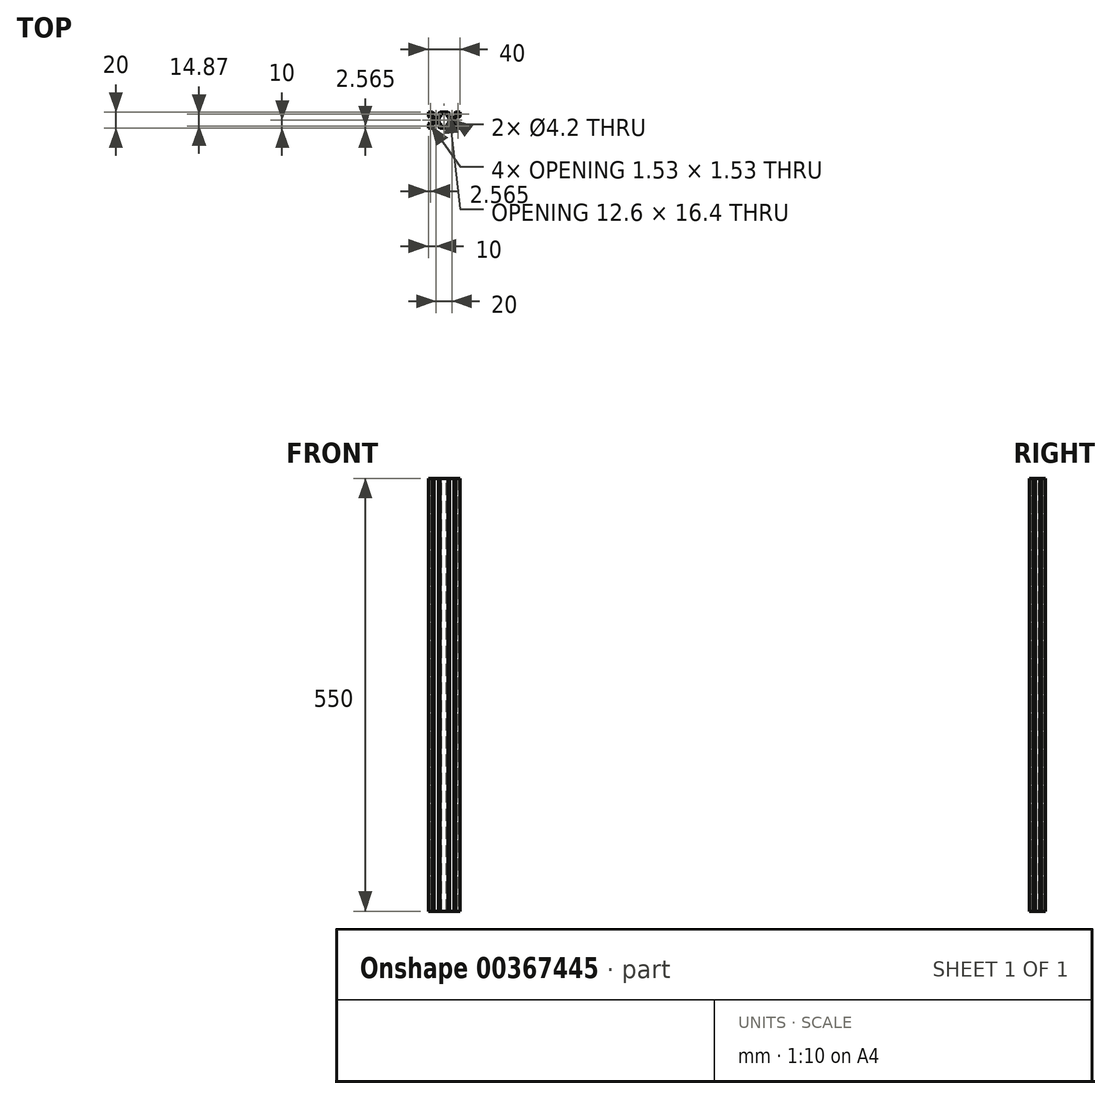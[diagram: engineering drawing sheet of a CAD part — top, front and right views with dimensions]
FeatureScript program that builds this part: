
annotation { "Feature Type Name" : "Feature", "Feature Type Description" : "" }
export const myFeature = defineFeature(function(context is Context, id is Id, definition is map)
    precondition{}
    {
        {
            var Q0;
            Q0=qCreatedBy(makeId("Top.planeOp"),FACE);
            var sketch = newSketch(context, id + "F0", { "sketchPlane" : qUnion([Q0])});
            skLineSegment(sketch, "E0.bottom", {"start": v(0, 0) * mm, "end": v(5.2, 0) * mm});
            skLineSegment(sketch, "E0.top", {"start": v(0, 20) * mm, "end": v(5.2, 20) * mm});
            skLineSegment(sketch, "E0.left", {"start": v(0, 0) * mm, "end": v(0, 5.2) * mm});
            skLineSegment(sketch, "E0.right", {"start": v(40, 0) * mm, "end": v(40, 5.2) * mm});
            skLineSegment(sketch, "E1", {"start": v(33.8, 12.84) * mm, "end": v(33.8, 7.16) * mm});
            skLineSegment(sketch, "E2", {"start": v(33.8, 12.84) * mm, "end": v(36.56, 15.6) * mm});
            skLineSegment(sketch, "E3", {"start": v(33.8, 7.16) * mm, "end": v(36.56, 4.4) * mm});
            skLineSegment(sketch, "E4", {"start": v(36.56, 15.6) * mm, "end": v(38.2, 15.6) * mm});
            skLineSegment(sketch, "E5", {"start": v(36.56, 4.4) * mm, "end": v(38.2, 4.4) * mm});
            skLineSegment(sketch, "E6", {"start": v(38.2, 13) * mm, "end": v(38.2, 15.6) * mm});
            skLineSegment(sketch, "E7", {"start": v(38.2, 7) * mm, "end": v(38.2, 4.4) * mm});
            skLineSegment(sketch, "E8.trimOffspring", {"start": v(40, 14.8) * mm, "end": v(40, 20) * mm});
            skLineSegment(sketch, "E9", {"start": v(33, 18.2) * mm, "end": v(35.6, 18.2) * mm});
            skLineSegment(sketch, "E10", {"start": v(35.6, 18.2) * mm, "end": v(35.6, 16.56) * mm});
            skLineSegment(sketch, "E11", {"start": v(35.6, 16.56) * mm, "end": v(32.84, 13.8) * mm});
            skLineSegment(sketch, "E12", {"start": v(32.84, 13.8) * mm, "end": v(27.16, 13.8) * mm});
            skLineSegment(sketch, "E13", {"start": v(27, 18.2) * mm, "end": v(24.4, 18.2) * mm});
            skLineSegment(sketch, "E14", {"start": v(24.4, 18.2) * mm, "end": v(24.4, 16.56) * mm});
            skLineSegment(sketch, "E15", {"start": v(24.4, 16.56) * mm, "end": v(27.16, 13.8) * mm});
            skLineSegment(sketch, "E16", {"start": v(33, 1.8) * mm, "end": v(35.6, 1.8) * mm});
            skLineSegment(sketch, "E17", {"start": v(35.6, 1.8) * mm, "end": v(35.6, 3.44) * mm});
            skLineSegment(sketch, "E18", {"start": v(35.6, 3.44) * mm, "end": v(32.84, 6.2) * mm});
            skLineSegment(sketch, "E19", {"start": v(32.84, 6.2) * mm, "end": v(27.16, 6.2) * mm});
            skLineSegment(sketch, "E20", {"start": v(27.16, 6.2) * mm, "end": v(24.4, 3.44) * mm});
            skLineSegment(sketch, "E21", {"start": v(24.4, 3.44) * mm, "end": v(24.4, 1.8) * mm});
            skLineSegment(sketch, "E22", {"start": v(24.4, 1.8) * mm, "end": v(27, 1.8) * mm});
            skLineSegment(sketch, "E23.trimOffspring", {"start": v(34.8, 20) * mm, "end": v(40, 20) * mm});
            skLineSegment(sketch, "E24.trimOffspring", {"start": v(34.8, 0) * mm, "end": v(40, 0) * mm});
            skLineSegment(sketch, "E25", {"start": v(7, 18.2) * mm, "end": v(4.4, 18.2) * mm});
            skLineSegment(sketch, "E26", {"start": v(4.4, 18.2) * mm, "end": v(4.4, 16.56) * mm});
            skLineSegment(sketch, "E27", {"start": v(4.4, 16.56) * mm, "end": v(7.16, 13.8) * mm});
            skLineSegment(sketch, "E28", {"start": v(7.16, 13.8) * mm, "end": v(12.84, 13.8) * mm});
            skLineSegment(sketch, "E29", {"start": v(12.84, 13.8) * mm, "end": v(15.6, 16.56) * mm});
            skLineSegment(sketch, "E30", {"start": v(15.6, 16.56) * mm, "end": v(15.6, 18.2) * mm});
            skLineSegment(sketch, "E31", {"start": v(15.6, 18.2) * mm, "end": v(13, 18.2) * mm});
            skLineSegment(sketch, "E32", {"start": v(1.8, 13) * mm, "end": v(1.8, 15.6) * mm});
            skLineSegment(sketch, "E33", {"start": v(1.8, 15.6) * mm, "end": v(3.44, 15.6) * mm});
            skLineSegment(sketch, "E34", {"start": v(3.44, 15.6) * mm, "end": v(6.2, 12.84) * mm});
            skLineSegment(sketch, "E35", {"start": v(6.2, 12.84) * mm, "end": v(6.2, 7.16) * mm});
            skLineSegment(sketch, "E36", {"start": v(6.2, 7.16) * mm, "end": v(3.44, 4.4) * mm});
            skLineSegment(sketch, "E37", {"start": v(3.44, 4.4) * mm, "end": v(1.8, 4.4) * mm});
            skLineSegment(sketch, "E38", {"start": v(1.8, 7) * mm, "end": v(1.8, 4.4) * mm});
            skLineSegment(sketch, "E39", {"start": v(7, 1.8) * mm, "end": v(4.4, 1.8) * mm});
            skLineSegment(sketch, "E40", {"start": v(4.4, 1.8) * mm, "end": v(4.4, 3.44) * mm});
            skLineSegment(sketch, "E41", {"start": v(4.4, 3.44) * mm, "end": v(7.16, 6.2) * mm});
            skLineSegment(sketch, "E42", {"start": v(7.16, 6.2) * mm, "end": v(12.84, 6.2) * mm});
            skLineSegment(sketch, "E43", {"start": v(12.84, 6.2) * mm, "end": v(15.6, 3.44) * mm});
            skLineSegment(sketch, "E44", {"start": v(15.6, 3.44) * mm, "end": v(15.6, 1.8) * mm});
            skLineSegment(sketch, "E45", {"start": v(15.6, 1.8) * mm, "end": v(13, 1.8) * mm});
            skLineSegment(sketch, "E46.trimOffspring", {"start": v(14.8, 20) * mm, "end": v(25.2, 20) * mm});
            skLineSegment(sketch, "E47.trimOffspring", {"start": v(0, 14.8) * mm, "end": v(0, 20) * mm});
            skLineSegment(sketch, "E48.trimOffspring", {"start": v(14.8, 0) * mm, "end": v(25.2, 0) * mm});
            skLineSegment(sketch, "E49", {"start": v(38.2, 7) * mm, "end": v(40, 5.2) * mm});
            skLineSegment(sketch, "E50", {"start": v(38.2, 13) * mm, "end": v(40, 14.8) * mm});
            skLineSegment(sketch, "E51", {"start": v(33, 1.8) * mm, "end": v(34.8, 0) * mm});
            skLineSegment(sketch, "E52", {"start": v(27, 1.8) * mm, "end": v(25.2, 0) * mm});
            skLineSegment(sketch, "E53", {"start": v(13, 1.8) * mm, "end": v(14.8, 0) * mm});
            skLineSegment(sketch, "E54", {"start": v(7, 1.8) * mm, "end": v(5.2, 0) * mm});
            skLineSegment(sketch, "E55", {"start": v(1.8, 7) * mm, "end": v(0, 5.2) * mm});
            skLineSegment(sketch, "E56", {"start": v(1.8, 13) * mm, "end": v(0, 14.8) * mm});
            skLineSegment(sketch, "E57", {"start": v(7, 18.2) * mm, "end": v(5.2, 20) * mm});
            skLineSegment(sketch, "E58", {"start": v(13, 18.2) * mm, "end": v(14.8, 20) * mm});
            skLineSegment(sketch, "E59", {"start": v(27, 18.2) * mm, "end": v(25.2, 20) * mm});
            skLineSegment(sketch, "E60", {"start": v(33, 18.2) * mm, "end": v(34.8, 20) * mm});
            skPoint(sketch, "E61.start.orphan", {"position": v(7, 0) * mm});
            skSolve(sketch);
        }
        {
            var Q0;
            Q0=qSketchRegion(id+"F0",true);
            extrude(context, id + "F1", {"entities" : qUnion([Q0]), "depth" : 1500 * mm});
        }
        {
            var Q0;
            Q0=makeQuery(id+"F1.opExtrude","CAP_FACE",FACE,{"disambiguationData":[OSD([sQuery(id+"F0.wireOp",EDGE,"E0.bottom"),sQuery(id+"F0.wireOp",EDGE,"E0.top"),sQuery(id+"F0.wireOp",EDGE,"E0.left"),sQuery(id+"F0.wireOp",EDGE,"E0.right"),sQuery(id+"F0.wireOp",EDGE,"E1"),sQuery(id+"F0.wireOp",EDGE,"E2"),sQuery(id+"F0.wireOp",EDGE,"E3"),sQuery(id+"F0.wireOp",EDGE,"E4"),sQuery(id+"F0.wireOp",EDGE,"E5"),sQuery(id+"F0.wireOp",EDGE,"E6"),sQuery(id+"F0.wireOp",EDGE,"E7"),sQuery(id+"F0.wireOp",EDGE,"E8.trimOffspring"),sQuery(id+"F0.wireOp",EDGE,"E9"),sQuery(id+"F0.wireOp",EDGE,"E10"),sQuery(id+"F0.wireOp",EDGE,"E11"),sQuery(id+"F0.wireOp",EDGE,"E12"),sQuery(id+"F0.wireOp",EDGE,"E13"),sQuery(id+"F0.wireOp",EDGE,"E14"),sQuery(id+"F0.wireOp",EDGE,"E15"),sQuery(id+"F0.wireOp",EDGE,"E16"),sQuery(id+"F0.wireOp",EDGE,"E17"),sQuery(id+"F0.wireOp",EDGE,"E18"),sQuery(id+"F0.wireOp",EDGE,"E19"),sQuery(id+"F0.wireOp",EDGE,"E20"),sQuery(id+"F0.wireOp",EDGE,"E21"),sQuery(id+"F0.wireOp",EDGE,"E22"),sQuery(id+"F0.wireOp",EDGE,"E23.trimOffspring"),sQuery(id+"F0.wireOp",EDGE,"E24.trimOffspring"),sQuery(id+"F0.wireOp",EDGE,"E25"),sQuery(id+"F0.wireOp",EDGE,"E26"),sQuery(id+"F0.wireOp",EDGE,"E27"),sQuery(id+"F0.wireOp",EDGE,"E28"),sQuery(id+"F0.wireOp",EDGE,"E29"),sQuery(id+"F0.wireOp",EDGE,"E30"),sQuery(id+"F0.wireOp",EDGE,"E31"),sQuery(id+"F0.wireOp",EDGE,"E32"),sQuery(id+"F0.wireOp",EDGE,"E33"),sQuery(id+"F0.wireOp",EDGE,"E34"),sQuery(id+"F0.wireOp",EDGE,"E35"),sQuery(id+"F0.wireOp",EDGE,"E36"),sQuery(id+"F0.wireOp",EDGE,"E37"),sQuery(id+"F0.wireOp",EDGE,"E38"),sQuery(id+"F0.wireOp",EDGE,"E39"),sQuery(id+"F0.wireOp",EDGE,"E40"),sQuery(id+"F0.wireOp",EDGE,"E41"),sQuery(id+"F0.wireOp",EDGE,"E42"),sQuery(id+"F0.wireOp",EDGE,"E43"),sQuery(id+"F0.wireOp",EDGE,"E44"),sQuery(id+"F0.wireOp",EDGE,"E45"),sQuery(id+"F0.wireOp",EDGE,"E46.trimOffspring"),sQuery(id+"F0.wireOp",EDGE,"E47.trimOffspring"),sQuery(id+"F0.wireOp",EDGE,"E48.trimOffspring"),sQuery(id+"F0.wireOp",EDGE,"E49"),sQuery(id+"F0.wireOp",EDGE,"E50"),sQuery(id+"F0.wireOp",EDGE,"E51"),sQuery(id+"F0.wireOp",EDGE,"E52"),sQuery(id+"F0.wireOp",EDGE,"E53"),sQuery(id+"F0.wireOp",EDGE,"E54"),sQuery(id+"F0.wireOp",EDGE,"E55"),sQuery(id+"F0.wireOp",EDGE,"E56"),sQuery(id+"F0.wireOp",EDGE,"E57"),sQuery(id+"F0.wireOp",EDGE,"E58"),sQuery(id+"F0.wireOp",EDGE,"E59"),sQuery(id+"F0.wireOp",EDGE,"E60")])],"isStart":false});
            var sketch = newSketch(context, id + "F2", { "sketchPlane" : qUnion([Q0])});
            skLineSegment(sketch, "E62", {"start": v(1.8, 18.2) * mm, "end": v(1.8, 16.67) * mm});
            skLineSegment(sketch, "E63", {"start": v(1.8, 16.67) * mm, "end": v(3.33, 18.2) * mm});
            skLineSegment(sketch, "E64", {"start": v(3.33, 18.2) * mm, "end": v(1.8, 18.2) * mm});
            skLineSegment(sketch, "E65", {"start": v(1.8, 1.8) * mm, "end": v(3.33, 1.8) * mm});
            skLineSegment(sketch, "E66", {"start": v(3.33, 1.8) * mm, "end": v(1.8, 3.33) * mm});
            skLineSegment(sketch, "E67", {"start": v(1.8, 3.33) * mm, "end": v(1.8, 1.8) * mm});
            skLineSegment(sketch, "E68", {"start": v(38.2, 1.8) * mm, "end": v(38.2, 3.33) * mm});
            skLineSegment(sketch, "E69", {"start": v(38.2, 3.33) * mm, "end": v(36.67, 1.8) * mm});
            skLineSegment(sketch, "E70", {"start": v(36.67, 1.8) * mm, "end": v(38.2, 1.8) * mm});
            skLineSegment(sketch, "E71", {"start": v(38.2, 18.2) * mm, "end": v(38.2, 16.67) * mm});
            skLineSegment(sketch, "E72", {"start": v(38.2, 16.67) * mm, "end": v(36.67, 18.2) * mm});
            skLineSegment(sketch, "E73", {"start": v(36.67, 18.2) * mm, "end": v(38.2, 18.2) * mm});
            skSolve(sketch);
        }
        {
            var Q0;
            Q0=qSketchRegion(id+"F2",true);
            extrude(context, id + "F3", {"entities" : qUnion([Q0]), "operationType" : NewBodyOperationType.REMOVE, "flatOperationType" : FlatOperationType.REMOVE, "endBound" : BoundingType.THROUGH_ALL, "oppositeDirection" : true, "offsetDistance" : 25 * mm, "depth" : 25 * mm, "domain" : OperationDomain.MODEL});
        }
        {
            var Q0;
            Q0=makeQuery(id+"F1.opExtrude","CAP_FACE",FACE,{"disambiguationData":[OSD([sQuery(id+"F0.wireOp",EDGE,"E0.bottom"),sQuery(id+"F0.wireOp",EDGE,"E0.top"),sQuery(id+"F0.wireOp",EDGE,"E0.left"),sQuery(id+"F0.wireOp",EDGE,"E0.right"),sQuery(id+"F0.wireOp",EDGE,"E1"),sQuery(id+"F0.wireOp",EDGE,"E2"),sQuery(id+"F0.wireOp",EDGE,"E3"),sQuery(id+"F0.wireOp",EDGE,"E4"),sQuery(id+"F0.wireOp",EDGE,"E5"),sQuery(id+"F0.wireOp",EDGE,"E6"),sQuery(id+"F0.wireOp",EDGE,"E7"),sQuery(id+"F0.wireOp",EDGE,"E8.trimOffspring"),sQuery(id+"F0.wireOp",EDGE,"E9"),sQuery(id+"F0.wireOp",EDGE,"E10"),sQuery(id+"F0.wireOp",EDGE,"E11"),sQuery(id+"F0.wireOp",EDGE,"E12"),sQuery(id+"F0.wireOp",EDGE,"E13"),sQuery(id+"F0.wireOp",EDGE,"E14"),sQuery(id+"F0.wireOp",EDGE,"E15"),sQuery(id+"F0.wireOp",EDGE,"E16"),sQuery(id+"F0.wireOp",EDGE,"E17"),sQuery(id+"F0.wireOp",EDGE,"E18"),sQuery(id+"F0.wireOp",EDGE,"E19"),sQuery(id+"F0.wireOp",EDGE,"E20"),sQuery(id+"F0.wireOp",EDGE,"E21"),sQuery(id+"F0.wireOp",EDGE,"E22"),sQuery(id+"F0.wireOp",EDGE,"E23.trimOffspring"),sQuery(id+"F0.wireOp",EDGE,"E24.trimOffspring"),sQuery(id+"F0.wireOp",EDGE,"E25"),sQuery(id+"F0.wireOp",EDGE,"E26"),sQuery(id+"F0.wireOp",EDGE,"E27"),sQuery(id+"F0.wireOp",EDGE,"E28"),sQuery(id+"F0.wireOp",EDGE,"E29"),sQuery(id+"F0.wireOp",EDGE,"E30"),sQuery(id+"F0.wireOp",EDGE,"E31"),sQuery(id+"F0.wireOp",EDGE,"E32"),sQuery(id+"F0.wireOp",EDGE,"E33"),sQuery(id+"F0.wireOp",EDGE,"E34"),sQuery(id+"F0.wireOp",EDGE,"E35"),sQuery(id+"F0.wireOp",EDGE,"E36"),sQuery(id+"F0.wireOp",EDGE,"E37"),sQuery(id+"F0.wireOp",EDGE,"E38"),sQuery(id+"F0.wireOp",EDGE,"E39"),sQuery(id+"F0.wireOp",EDGE,"E40"),sQuery(id+"F0.wireOp",EDGE,"E41"),sQuery(id+"F0.wireOp",EDGE,"E42"),sQuery(id+"F0.wireOp",EDGE,"E43"),sQuery(id+"F0.wireOp",EDGE,"E44"),sQuery(id+"F0.wireOp",EDGE,"E45"),sQuery(id+"F0.wireOp",EDGE,"E46.trimOffspring"),sQuery(id+"F0.wireOp",EDGE,"E47.trimOffspring"),sQuery(id+"F0.wireOp",EDGE,"E48.trimOffspring"),sQuery(id+"F0.wireOp",EDGE,"E49"),sQuery(id+"F0.wireOp",EDGE,"E50"),sQuery(id+"F0.wireOp",EDGE,"E51"),sQuery(id+"F0.wireOp",EDGE,"E52"),sQuery(id+"F0.wireOp",EDGE,"E53"),sQuery(id+"F0.wireOp",EDGE,"E54"),sQuery(id+"F0.wireOp",EDGE,"E55"),sQuery(id+"F0.wireOp",EDGE,"E56"),sQuery(id+"F0.wireOp",EDGE,"E57"),sQuery(id+"F0.wireOp",EDGE,"E58"),sQuery(id+"F0.wireOp",EDGE,"E59"),sQuery(id+"F0.wireOp",EDGE,"E60")])],"isStart":false});
            var sketch = newSketch(context, id + "F4", { "sketchPlane" : qUnion([Q0])});
            skLineSegment(sketch, "E74", {"start": v(17.1, 18.2) * mm, "end": v(22.9, 18.2) * mm});
            skLineSegment(sketch, "E75", {"start": v(22.9, 1.8) * mm, "end": v(17.1, 1.8) * mm});
            skLineSegment(sketch, "E76", {"start": v(17.1, 1.8) * mm, "end": v(17.1, 3.76) * mm});
            skLineSegment(sketch, "E77", {"start": v(22.9, 1.8) * mm, "end": v(22.9, 3.76) * mm});
            skLineSegment(sketch, "E78", {"start": v(22.9, 18.2) * mm, "end": v(22.9, 16.24) * mm});
            skLineSegment(sketch, "E79", {"start": v(17.1, 18.2) * mm, "end": v(17.1, 16.24) * mm});
            skLineSegment(sketch, "E80", {"start": v(22.9, 16.24) * mm, "end": v(26.3, 12.84) * mm});
            skLineSegment(sketch, "E81", {"start": v(26.3, 12.84) * mm, "end": v(26.3, 7.16) * mm});
            skLineSegment(sketch, "E82", {"start": v(26.3, 7.16) * mm, "end": v(22.9, 3.76) * mm});
            skLineSegment(sketch, "E83", {"start": v(17.1, 3.76) * mm, "end": v(13.7, 7.16) * mm});
            skLineSegment(sketch, "E84", {"start": v(13.7, 7.16) * mm, "end": v(13.7, 12.84) * mm});
            skLineSegment(sketch, "E85", {"start": v(13.7, 12.84) * mm, "end": v(17.1, 16.24) * mm});
            skCircle(sketch, "E86", {"center": v(30, 10) * mm, "radius": 2.1 * mm});
            skPoint(sketch, "E86.centerSnap0", {"position": v(30, 13.8) * mm});
            skPoint(sketch, "E86.centerSnap1", {"position": v(26.3, 10) * mm});
            skCircle(sketch, "E87", {"center": v(10, 10) * mm, "radius": 2.1 * mm});
            skPoint(sketch, "E87.centerSnap0", {"position": v(10, 13.8) * mm});
            skPoint(sketch, "E87.centerSnap1", {"position": v(13.7, 10) * mm});
            skSolve(sketch);
        }
        {
            var Q0;
            Q0=qSketchRegion(id+"F4",true);
            extrude(context, id + "F5", {"entities" : qUnion([Q0]), "operationType" : NewBodyOperationType.REMOVE, "endBound" : BoundingType.THROUGH_ALL, "oppositeDirection" : true, "depth" : 25 * mm});
        }
        {
            var Q0;
            Q0=makeQuery(id+"F1.opExtrude","CAP_FACE",FACE,{"disambiguationData":[OSD([sQuery(id+"F0.wireOp",EDGE,"E0.bottom"),sQuery(id+"F0.wireOp",EDGE,"E0.top"),sQuery(id+"F0.wireOp",EDGE,"E0.left"),sQuery(id+"F0.wireOp",EDGE,"E0.right"),sQuery(id+"F0.wireOp",EDGE,"E1"),sQuery(id+"F0.wireOp",EDGE,"E2"),sQuery(id+"F0.wireOp",EDGE,"E3"),sQuery(id+"F0.wireOp",EDGE,"E4"),sQuery(id+"F0.wireOp",EDGE,"E5"),sQuery(id+"F0.wireOp",EDGE,"E6"),sQuery(id+"F0.wireOp",EDGE,"E7"),sQuery(id+"F0.wireOp",EDGE,"E8.trimOffspring"),sQuery(id+"F0.wireOp",EDGE,"E9"),sQuery(id+"F0.wireOp",EDGE,"E10"),sQuery(id+"F0.wireOp",EDGE,"E11"),sQuery(id+"F0.wireOp",EDGE,"E12"),sQuery(id+"F0.wireOp",EDGE,"E13"),sQuery(id+"F0.wireOp",EDGE,"E14"),sQuery(id+"F0.wireOp",EDGE,"E15"),sQuery(id+"F0.wireOp",EDGE,"E16"),sQuery(id+"F0.wireOp",EDGE,"E17"),sQuery(id+"F0.wireOp",EDGE,"E18"),sQuery(id+"F0.wireOp",EDGE,"E19"),sQuery(id+"F0.wireOp",EDGE,"E20"),sQuery(id+"F0.wireOp",EDGE,"E21"),sQuery(id+"F0.wireOp",EDGE,"E22"),sQuery(id+"F0.wireOp",EDGE,"E23.trimOffspring"),sQuery(id+"F0.wireOp",EDGE,"E24.trimOffspring"),sQuery(id+"F0.wireOp",EDGE,"E25"),sQuery(id+"F0.wireOp",EDGE,"E26"),sQuery(id+"F0.wireOp",EDGE,"E27"),sQuery(id+"F0.wireOp",EDGE,"E28"),sQuery(id+"F0.wireOp",EDGE,"E29"),sQuery(id+"F0.wireOp",EDGE,"E30"),sQuery(id+"F0.wireOp",EDGE,"E31"),sQuery(id+"F0.wireOp",EDGE,"E32"),sQuery(id+"F0.wireOp",EDGE,"E33"),sQuery(id+"F0.wireOp",EDGE,"E34"),sQuery(id+"F0.wireOp",EDGE,"E35"),sQuery(id+"F0.wireOp",EDGE,"E36"),sQuery(id+"F0.wireOp",EDGE,"E37"),sQuery(id+"F0.wireOp",EDGE,"E38"),sQuery(id+"F0.wireOp",EDGE,"E39"),sQuery(id+"F0.wireOp",EDGE,"E40"),sQuery(id+"F0.wireOp",EDGE,"E41"),sQuery(id+"F0.wireOp",EDGE,"E42"),sQuery(id+"F0.wireOp",EDGE,"E43"),sQuery(id+"F0.wireOp",EDGE,"E44"),sQuery(id+"F0.wireOp",EDGE,"E45"),sQuery(id+"F0.wireOp",EDGE,"E46.trimOffspring"),sQuery(id+"F0.wireOp",EDGE,"E47.trimOffspring"),sQuery(id+"F0.wireOp",EDGE,"E48.trimOffspring"),sQuery(id+"F0.wireOp",EDGE,"E49"),sQuery(id+"F0.wireOp",EDGE,"E50"),sQuery(id+"F0.wireOp",EDGE,"E51"),sQuery(id+"F0.wireOp",EDGE,"E52"),sQuery(id+"F0.wireOp",EDGE,"E53"),sQuery(id+"F0.wireOp",EDGE,"E54"),sQuery(id+"F0.wireOp",EDGE,"E55"),sQuery(id+"F0.wireOp",EDGE,"E56"),sQuery(id+"F0.wireOp",EDGE,"E57"),sQuery(id+"F0.wireOp",EDGE,"E58"),sQuery(id+"F0.wireOp",EDGE,"E59"),sQuery(id+"F0.wireOp",EDGE,"E60")])],"isStart":false});
            extrude(context, id + "F6", {"entities" : qUnion([Q0]), "operationType" : NewBodyOperationType.REMOVE, "oppositeDirection" : true, "depth" : 950 * mm});
        }
    });
